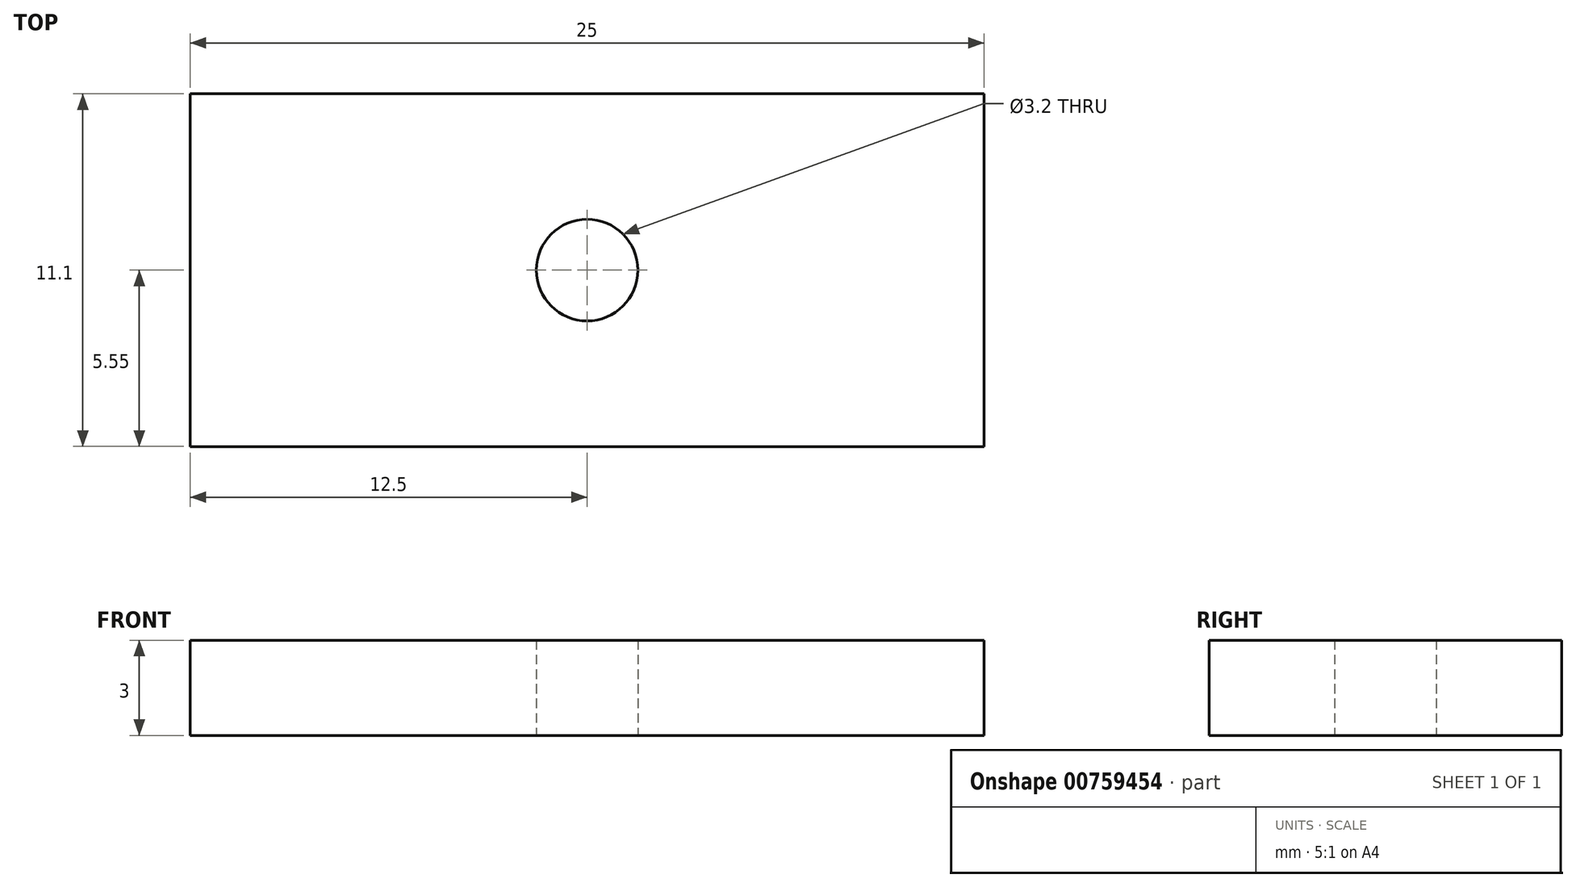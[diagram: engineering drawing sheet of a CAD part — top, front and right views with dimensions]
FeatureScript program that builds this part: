
annotation { "Feature Type Name" : "Feature", "Feature Type Description" : "" }
export const myFeature = defineFeature(function(context is Context, id is Id, definition is map)
    precondition{}
    {
        {
            var Q0;
            Q0=qCreatedBy(makeId("Top.planeOp"),FACE);
            var sketch = newSketch(context, id + "F0", { "sketchPlane" : qUnion([Q0])});
            skLineSegment(sketch, "E0.bottom", {"start": v(-12.5, 5.56) * mm, "end": v(12.5, 5.56) * mm});
            skLineSegment(sketch, "E0.top", {"start": v(-12.5, -5.56) * mm, "end": v(12.5, -5.56) * mm});
            skLineSegment(sketch, "E0.left", {"start": v(-12.5, 5.56) * mm, "end": v(-12.5, -5.56) * mm});
            skLineSegment(sketch, "E0.right", {"start": v(12.5, 5.56) * mm, "end": v(12.5, -5.56) * mm});
            skPoint(sketch, "E0.middle", {"position": v(0, 0) * mm});
            skCircle(sketch, "E1", {"center": v(0, 0) * mm, "radius": 1.6 * mm});
            skSolve(sketch);
        }
        {
            var Q0;
            Q0=makeQuery(id+"F0.imprint","IMPRINT",FACE,{"disambiguationData":[TD([[makeQuery(id+"F0.imprint","IMPRINT",EDGE,{"derivedFrom":sQuery(id+"F0.wireOp",EDGE,"E0.bottom")}),-1.0]])]});
            extrude(context, id + "F1", {"entities" : qUnion([Q0]), "depth" : 3 * mm, "offsetDistance" : 25 * mm});
        }
    });
